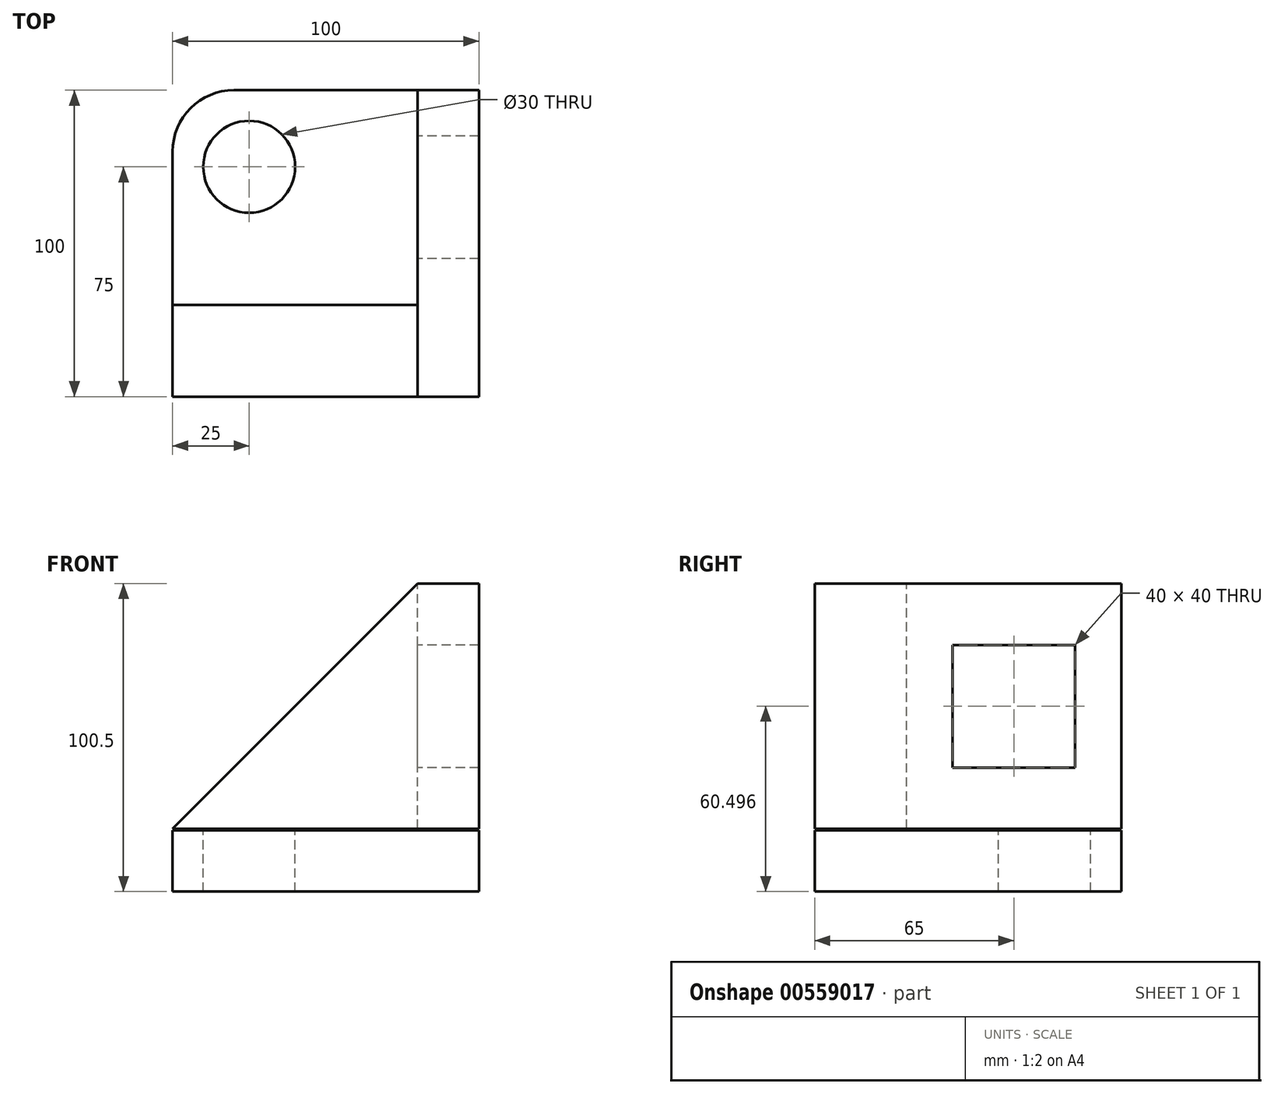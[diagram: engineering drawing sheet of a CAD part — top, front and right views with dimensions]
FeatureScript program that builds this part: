
annotation { "Feature Type Name" : "Feature", "Feature Type Description" : "" }
export const myFeature = defineFeature(function(context is Context, id is Id, definition is map)
    precondition{}
    {
        {
            var Q0;
            Q0=qCreatedBy(makeId("Top.planeOp"),FACE);
            var sketch = newSketch(context, id + "F0", { "sketchPlane" : qUnion([Q0])});
            skLineSegment(sketch, "E0.bottom", {"start": v(-100, 0) * mm, "end": v(0, 0) * mm});
            skLineSegment(sketch, "E0.top", {"start": v(-100, -100) * mm, "end": v(0, -100) * mm});
            skLineSegment(sketch, "E0.left", {"start": v(-100, 0) * mm, "end": v(-100, -100) * mm});
            skLineSegment(sketch, "E0.right", {"start": v(0, 0) * mm, "end": v(0, -100) * mm});
            skSolve(sketch);
        }
        {
            var Q0;
            Q0 = qSketchRegion(id + "F0", true);
            extrude(context, id + "F1", {"entities" : qUnion([Q0]), "depth" : 20 * mm, "offsetDistance" : 25 * mm});
        }
        {
            var Q0;
            Q0=qCreatedBy(makeId("Right.planeOp"),FACE);
            var sketch = newSketch(context, id + "F2", { "sketchPlane" : qUnion([Q0])});
            skLineSegment(sketch, "E1.bottom", {"start": v(0, 20.5) * mm, "end": v(-100, 20.5) * mm});
            skLineSegment(sketch, "E1.top", {"start": v(0, 100.5) * mm, "end": v(-100, 100.5) * mm});
            skLineSegment(sketch, "E1.left", {"start": v(0, 20.5) * mm, "end": v(0, 100.5) * mm});
            skLineSegment(sketch, "E1.right", {"start": v(-100, 20.5) * mm, "end": v(-100, 100.5) * mm});
            skSolve(sketch);
        }
        {
            var Q0;
            Q0=makeQuery(id+"F2.imprint","IMPRINT",FACE,{"disambiguationData":[TD([[makeQuery(id+"F2.imprint","IMPRINT",EDGE,{"derivedFrom":sQuery(id+"F2.wireOp",EDGE,"E1.bottom")}),-1.0]])]});
            extrude(context, id + "F3", {"entities" : qUnion([Q0]), "oppositeDirection" : true, "depth" : 20 * mm, "offsetDistance" : 25 * mm});
        }
        {
            var Q0;
            Q0=makeQuery(id+"F1.opExtrude","CAP_FACE",FACE,{"disambiguationData":[OSD([sQuery(id+"F0.wireOp",EDGE,"E0.bottom"),sQuery(id+"F0.wireOp",EDGE,"E0.top"),sQuery(id+"F0.wireOp",EDGE,"E0.left"),sQuery(id+"F0.wireOp",EDGE,"E0.right")])],"isStart":false});
            var sketch = newSketch(context, id + "F4", { "sketchPlane" : qUnion([Q0])});
            skCircle(sketch, "E2", {"center": v(-75, -25) * mm, "radius": 15 * mm});
            skSolve(sketch);
        }
        {
            var Q0;
            Q0 = qSketchRegion(id + "F4", true);
            extrude(context, id + "F5", {"entities" : qUnion([Q0]), "operationType" : NewBodyOperationType.REMOVE, "oppositeDirection" : true, "depth" : 21 * mm, "offsetDistance" : 25 * mm});
        }
        {
            var Q0;
            Q0=makeQuery(id+"F3.opExtrude","SWEPT_FACE",FACE,{"disambiguationData":[OSD([sQuery(id+"F2.wireOp",EDGE,"E1.right")])]});
            var sketch = newSketch(context, id + "F6", { "sketchPlane" : qUnion([Q0])});
            skLineSegment(sketch, "E3.bottom", {"start": v(-20, 20.5) * mm, "end": v(-100, 20.5) * mm});
            skLineSegment(sketch, "E3.top", {"start": v(-20, 100.5) * mm, "end": v(-100, 100.5) * mm});
            skLineSegment(sketch, "E3.left", {"start": v(-20, 20.5) * mm, "end": v(-20, 100.5) * mm});
            skLineSegment(sketch, "E3.right", {"start": v(-100, 20.5) * mm, "end": v(-100, 100.5) * mm});
            skSolve(sketch);
        }
        {
            var Q0;
            Q0=makeQuery(id+"F6.imprint","IMPRINT",FACE,{"disambiguationData":[TD([[makeQuery(id+"F6.imprint","IMPRINT",EDGE,{"derivedFrom":sQuery(id+"F6.wireOp",EDGE,"E3.bottom")}),-1.0]])]});
            extrude(context, id + "F7", {"entities" : qUnion([Q0]), "operationType" : NewBodyOperationType.ADD, "oppositeDirection" : true, "depth" : 30 * mm, "offsetDistance" : 25 * mm});
        }
        {
            var Q0;
            Q0=makeQuery(id+"F7.opExtrude","SWEPT_EDGE",EDGE,{"disambiguationData":[OSD([sQuery(id+"F6.wireOp",EDGE,"E3.top"),sQuery(id+"F6.wireOp",EDGE,"E3.right")])]});
            chamfer(context, id + "F8", {"entities" : qUnion([Q0]), "width" : 80 * mm, "tangentPropagation" : true});
        }
        {
            var Q0;
            Q0=makeQuery(id+"F3.opExtrude","CAP_FACE",FACE,{"disambiguationData":[OSD([sQuery(id+"F2.wireOp",EDGE,"E1.bottom"),sQuery(id+"F2.wireOp",EDGE,"E1.top"),sQuery(id+"F2.wireOp",EDGE,"E1.left"),sQuery(id+"F2.wireOp",EDGE,"E1.right")])],"isStart":false});
            var sketch = newSketch(context, id + "F9", { "sketchPlane" : qUnion([Q0])});
            skLineSegment(sketch, "E4.bottom", {"start": v(55, 40.5) * mm, "end": v(15, 40.5) * mm});
            skLineSegment(sketch, "E4.top", {"start": v(55, 80.5) * mm, "end": v(15, 80.5) * mm});
            skLineSegment(sketch, "E4.left", {"start": v(55, 40.5) * mm, "end": v(55, 80.5) * mm});
            skLineSegment(sketch, "E4.right", {"start": v(15, 40.5) * mm, "end": v(15, 80.5) * mm});
            skPoint(sketch, "E4.middle", {"position": v(35, 60.5) * mm});
            skSolve(sketch);
        }
        {
            var Q0;
            Q0=makeQuery(id+"F9.imprint","IMPRINT",FACE,{"disambiguationData":[TD([[makeQuery(id+"F9.imprint","IMPRINT",EDGE,{"derivedFrom":sQuery(id+"F9.wireOp",EDGE,"E4.bottom")}),-1.0]])]});
            extrude(context, id + "F10", {"entities" : qUnion([Q0]), "operationType" : NewBodyOperationType.REMOVE, "oppositeDirection" : true, "depth" : 22 * mm, "offsetDistance" : 25 * mm});
        }
        {
            var Q0;
            Q0=makeQuery(id+"F1.opExtrude","SWEPT_EDGE",EDGE,{"disambiguationData":[OSD([sQuery(id+"F0.wireOp",EDGE,"E0.bottom"),sQuery(id+"F0.wireOp",EDGE,"E0.left")])]});
            fillet(context, id + "F11", {"entities" : qUnion([Q0]), "radius" : 20 * mm, "tangentPropagation" : true, "allowEdgeOverflow" : false});
        }
    });
